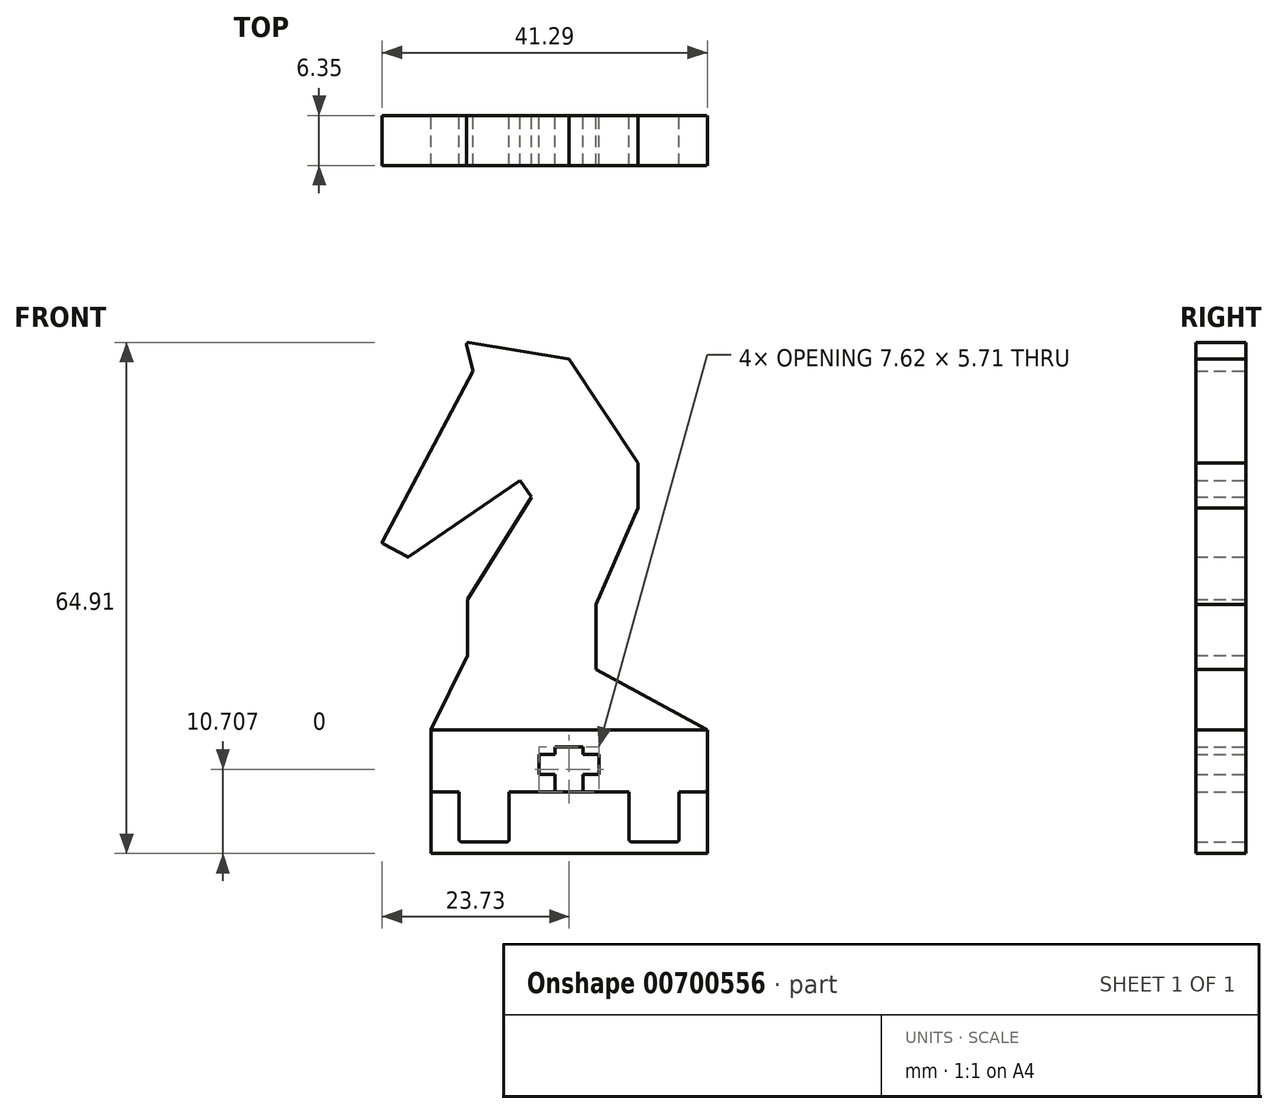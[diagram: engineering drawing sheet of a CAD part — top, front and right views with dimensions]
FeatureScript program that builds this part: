
annotation { "Feature Type Name" : "Feature", "Feature Type Description" : "" }
export const myFeature = defineFeature(function(context is Context, id is Id, definition is map)
    precondition{}
    {
        {
            var Q0;
            Q0=qCreatedBy(makeId("Front.planeOp"),FACE);
            var sketch = newSketch(context, id + "F0", { "sketchPlane" : qUnion([Q0])});
            skLineSegment(sketch, "E0.bottom", {"start": v(17.56, 7.85) * mm, "end": v(-17.56, 7.85) * mm});
            skLineSegment(sketch, "E0.top", {"start": v(17.56, -7.85) * mm, "end": v(-17.56, -7.85) * mm});
            skLineSegment(sketch, "E0.left", {"start": v(17.56, 7.85) * mm, "end": v(17.56, -7.85) * mm});
            skLineSegment(sketch, "E0.right", {"start": v(-17.56, 7.85) * mm, "end": v(-17.56, -7.85) * mm});
            skPoint(sketch, "E0.middle", {"position": v(0, 0) * mm});
            skSolve(sketch);
        }
        {
            var Q0;
            Q0=makeQuery(id+"F0.imprint","IMPRINT",FACE,{"disambiguationData":[TD([[makeQuery(id+"F0.imprint","IMPRINT",EDGE,{"derivedFrom":sQuery(id+"F0.wireOp",EDGE,"E0.bottom")}),1.0]])]});
            extrude(context, id + "F1", {"entities" : qUnion([Q0]), "depth" : 6.35 * mm, "offsetDistance" : 25.4 * mm});
        }
        {
            var Q0;
            Q0=makeQuery(id+"F0.imprint","IMPRINT",FACE,{"disambiguationData":[TD([[makeQuery(id+"F0.imprint","IMPRINT",EDGE,{"derivedFrom":sQuery(id+"F0.wireOp",EDGE,"E0.bottom")}),1.0]])]});
            var sketch = newSketch(context, id + "F2", { "sketchPlane" : qUnion([Q0])});
            skLineSegment(sketch, "E1", {"start": v(-17.53, 7.9) * mm, "end": v(-12.9, 17.33) * mm});
            skLineSegment(sketch, "E2", {"start": v(-12.9, 17.33) * mm, "end": v(-12.9, 24.4) * mm});
            skLineSegment(sketch, "E3", {"start": v(-12.9, 24.4) * mm, "end": v(-4.8, 37.42) * mm});
            skLineSegment(sketch, "E4", {"start": v(-4.8, 37.42) * mm, "end": v(-6.24, 39.53) * mm});
            skLineSegment(sketch, "E5", {"start": v(-6.24, 39.53) * mm, "end": v(-20.33, 29.87) * mm});
            skLineSegment(sketch, "E6", {"start": v(-20.6, 29.86) * mm, "end": v(-23.6, 31.45) * mm});
            skLineSegment(sketch, "E7", {"start": v(-23.7, 31.8) * mm, "end": v(-12.2, 53.42) * mm});
            skLineSegment(sketch, "E8", {"start": v(-12.2, 53.42) * mm, "end": v(-13.02, 56.75) * mm});
            skLineSegment(sketch, "E9", {"start": v(-12.73, 57.06) * mm, "end": v(0, 54.98) * mm});
            skLineSegment(sketch, "E10", {"start": v(0, 54.98) * mm, "end": v(8.75, 41.76) * mm});
            skLineSegment(sketch, "E11", {"start": v(8.75, 41.76) * mm, "end": v(8.75, 36.07) * mm});
            skLineSegment(sketch, "E12", {"start": v(8.75, 36.07) * mm, "end": v(3.4, 23.81) * mm});
            skLineSegment(sketch, "E13", {"start": v(3.4, 23.81) * mm, "end": v(3.4, 15.53) * mm});
            skLineSegment(sketch, "E14", {"start": v(3.4, 15.53) * mm, "end": v(17.42, 7.93) * mm});
            skPoint(sketch, "E15", {"position": v(4.38, 48.37) * mm});
            skPoint(sketch, "E16", {"position": v(8.75, 38.91) * mm});
            skPoint(sketch, "E17", {"position": v(6.07, 29.94) * mm});
            skPoint(sketch, "E18", {"position": v(3.4, 21.84) * mm});
            skPoint(sketch, "E19", {"position": v(6.22, 14) * mm});
            skPoint(sketch, "E20", {"position": v(-6.56, 56.05) * mm});
            skPoint(sketch, "E21", {"position": v(-3.42, 55.54) * mm});
            skLineSegment(sketch, "E22", {"start": v(-17.56, 7.8) * mm, "end": v(-17.56, 0.25) * mm});
            skLineSegment(sketch, "E23", {"start": v(-17.3, 0) * mm, "end": v(-13.97, 0) * mm});
            skLineSegment(sketch, "E24", {"start": v(17.56, 0.25) * mm, "end": v(17.56, 7.7) * mm});
            skLineSegment(sketch, "E25.top", {"start": v(-7.87, -6.35) * mm, "end": v(-13.72, -6.35) * mm});
            skLineSegment(sketch, "E25.left", {"start": v(-7.62, 0) * mm, "end": v(-7.62, -6.1) * mm});
            skLineSegment(sketch, "E25.right", {"start": v(-13.97, 0) * mm, "end": v(-13.97, -6.1) * mm});
            skLineSegment(sketch, "E26.MirrorCS", {"start": v(7.62, 0) * mm, "end": v(7.62, -6.1) * mm});
            skLineSegment(sketch, "E27.MirrorCS", {"start": v(7.87, -6.35) * mm, "end": v(13.72, -6.35) * mm});
            skLineSegment(sketch, "E28.MirrorCS", {"start": v(13.97, 0) * mm, "end": v(13.97, -6.1) * mm});
            skLineSegment(sketch, "E29.trimOffspring", {"start": v(-7.62, 0) * mm, "end": v(7.62, 0) * mm});
            skLineSegment(sketch, "E30.trimOffspring", {"start": v(13.97, 0) * mm, "end": v(17.3, 0) * mm});
            skPoint(sketch, "E31.visualSharp", {"position": v(-13.11, 57.12) * mm});
            skArc(sketch, "E31.filletArc", {"start": v(-12.73, 57.06) * mm, "mid": v(-12.96, 56.98) * mm, "end": v(-13.02, 56.75) * mm});
            skPoint(sketch, "E32.visualSharp", {"position": v(-23.82, 31.57) * mm});
            skArc(sketch, "E32.filletArc", {"start": v(-23.7, 31.8) * mm, "mid": v(-23.72, 31.6) * mm, "end": v(-23.6, 31.45) * mm});
            skPoint(sketch, "E33.visualSharp", {"position": v(-20.46, 29.79) * mm});
            skArc(sketch, "E33.filletArc", {"start": v(-20.6, 29.86) * mm, "mid": v(-20.46, 29.83) * mm, "end": v(-20.33, 29.87) * mm});
            skPoint(sketch, "E34.visualSharp", {"position": v(17.56, 0) * mm});
            skArc(sketch, "E34.filletArc", {"start": v(17.3, 0) * mm, "mid": v(17.48, 0.07) * mm, "end": v(17.56, 0.25) * mm});
            skPoint(sketch, "E35.visualSharp", {"position": v(-17.56, 0) * mm});
            skArc(sketch, "E35.filletArc", {"start": v(-17.56, 0.25) * mm, "mid": v(-17.48, 0.07) * mm, "end": v(-17.3, 0) * mm});
            skPoint(sketch, "E36.visualSharp", {"position": v(17.56, 7.85) * mm});
            skArc(sketch, "E36.filletArc", {"start": v(17.56, 7.7) * mm, "mid": v(17.52, 7.83) * mm, "end": v(17.42, 7.93) * mm});
            skPoint(sketch, "E37.visualSharp", {"position": v(-17.56, 7.85) * mm});
            skArc(sketch, "E37.filletArc", {"start": v(-17.53, 7.9) * mm, "mid": v(-17.55, 7.85) * mm, "end": v(-17.56, 7.8) * mm});
            skPoint(sketch, "E38.visualSharp", {"position": v(-13.97, -6.35) * mm});
            skArc(sketch, "E38.filletArc", {"start": v(-13.97, -6.1) * mm, "mid": v(-13.9, -6.28) * mm, "end": v(-13.72, -6.35) * mm});
            skPoint(sketch, "E39.visualSharp", {"position": v(-7.62, -6.35) * mm});
            skArc(sketch, "E39.filletArc", {"start": v(-7.87, -6.35) * mm, "mid": v(-7.7, -6.28) * mm, "end": v(-7.62, -6.1) * mm});
            skPoint(sketch, "E40.visualSharp", {"position": v(7.62, -6.35) * mm});
            skArc(sketch, "E40.filletArc", {"start": v(7.62, -6.1) * mm, "mid": v(7.7, -6.28) * mm, "end": v(7.87, -6.35) * mm});
            skPoint(sketch, "E41.visualSharp", {"position": v(13.97, -6.35) * mm});
            skArc(sketch, "E41.filletArc", {"start": v(13.72, -6.35) * mm, "mid": v(13.9, -6.28) * mm, "end": v(13.97, -6.1) * mm});
            skSolve(sketch);
        }
        {
            var Q0;
            Q0=makeQuery(id+"F2.imprint","IMPRINT",FACE,{"disambiguationData":[TD([[makeQuery(id+"F2.imprint","IMPRINT",EDGE,{"derivedFrom":sQuery(id+"F2.wireOp",EDGE,"E1")}),-1.0]])]});
            var Q1;
            Q1=makeQuery(id+"F2.imprint","IMPRINT",FACE,{"disambiguationData":[TD([[makeQuery(id+"F2.imprint","IMPRINT",EDGE,{"derivedFrom":sQuery(id+"F2.wireOp",EDGE,"E22")}),1.0]])]});
            extrude(context, id + "F3", {"entities" : qUnion([Q0, Q1]), "depth" : 6.35 * mm, "offsetDistance" : 25.4 * mm});
        }
        {
            var Q0;
            Q0=qCreatedBy(makeId("Front.planeOp"),FACE);
            var sketch = newSketch(context, id + "F4", { "sketchPlane" : qUnion([Q0])});
            skLineSegment(sketch, "E42", {"start": v(-37.35, 18.63) * mm, "end": v(-37.35, 18.63) * mm});
            skLineSegment(sketch, "E43.bottom", {"start": v(-1.78, 5.72) * mm, "end": v(1.78, 5.72) * mm});
            skLineSegment(sketch, "E43.left", {"start": v(-1.78, 5.72) * mm, "end": v(-1.78, 4.76) * mm});
            skLineSegment(sketch, "E44", {"start": v(0, 5.72) * mm, "end": v(0, 9.6) * mm, "construction": true});
            skLineSegment(sketch, "E45.bottom", {"start": v(-1.78, 4.76) * mm, "end": v(-3.81, 4.76) * mm});
            skLineSegment(sketch, "E45.top", {"start": v(-1.78, 2.22) * mm, "end": v(-3.81, 2.22) * mm});
            skLineSegment(sketch, "E45.right", {"start": v(-3.81, 4.76) * mm, "end": v(-3.81, 2.22) * mm});
            skLineSegment(sketch, "E46.top", {"start": v(-1.78, 0) * mm, "end": v(1.78, 0) * mm});
            skLineSegment(sketch, "E46.left", {"start": v(-1.78, 2.22) * mm, "end": v(-1.78, 0) * mm});
            skLineSegment(sketch, "E47.MirrorCS", {"start": v(3.8, 4.76) * mm, "end": v(3.8, 2.22) * mm});
            skLineSegment(sketch, "E48.MirrorCS", {"start": v(1.78, 5.72) * mm, "end": v(1.78, 4.76) * mm});
            skLineSegment(sketch, "E49.MirrorCS", {"start": v(1.78, 2.22) * mm, "end": v(1.78, 0) * mm});
            skLineSegment(sketch, "E50.MirrorCS", {"start": v(1.78, 4.76) * mm, "end": v(3.8, 4.76) * mm});
            skLineSegment(sketch, "E51.MirrorCS", {"start": v(1.78, 0) * mm, "end": v(-1.78, 0) * mm});
            skLineSegment(sketch, "E52.MirrorCS", {"start": v(1.78, 2.22) * mm, "end": v(3.8, 2.22) * mm});
            skLineSegment(sketch, "E53.MirrorCS", {"start": v(1.78, 5.72) * mm, "end": v(-1.78, 5.72) * mm});
            skSolve(sketch);
        }
        {
            var Q0;
            Q0 = qSketchRegion(id + "F4", true);
            extrude(context, id + "F5", {"entities" : qUnion([Q0]), "operationType" : NewBodyOperationType.REMOVE, "depth" : 25.4 * mm, "offsetDistance" : 25.4 * mm});
        }
    });
